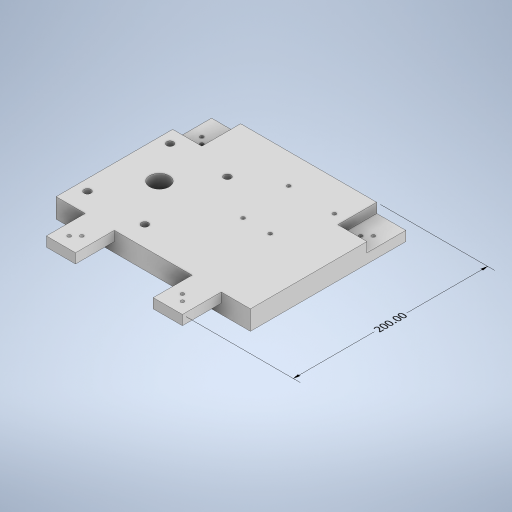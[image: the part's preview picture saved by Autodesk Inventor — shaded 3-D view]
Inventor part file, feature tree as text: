
AUTODESK INVENTOR PART (.ipt)
format: ipt  version: 2023 (Build 270158000, 158)  size: 358,912 bytes
history: native  units: mm
features: sketch x7, extrude x4, other x3, hole x3
ambient origin geometry x8: Origin, YZ Plane, XZ Plane, XY Plane, X Axis, Y Axis, Z Axis, Center Point
bodies: Body1 (feature_tree)
feature tree (17):
  other  "Sólido1"
  other  "Anotaciones"
  extrude  "Extrusión1"  Depth=160.0mm
  extrude  "Extrusión2"  Depth=30.0mm
  hole  "Agujero1"  [1 undecoded]
  extrude  "Extrusión3"  Depth=11.75mm
  hole  "Agujero2"  [1 undecoded]
  hole  "Agujero3"  [1 undecoded]
  extrude  "Extrusión4"  Depth=40.0mm TaperAngle=0.0deg
  sketch  "Boceto1"  dims[d0=200.0mm d1=160.0mm]
  sketch  "Boceto2"  dims[d2=20.0mm d3=0.0mm d4=30.0mm]
  sketch  "Boceto3"  dims[d5=40.0mm d6=10.0mm d7=0.0mm]
  sketch  "Boceto4"  dims[d23=21.75mm d24=11.75mm]
  sketch  "Boceto5"  dims[d26=11.75mm]
  sketch  "Boceto6"  dims[d27=3.5mm d28=6.0mm d29=4.0mm d30=2.0mm d31=90.0deg d32=8.0mm d33=20.594885mm d34=30.0mm]
  sketch  "Boceto7"  dims[d35=10.0mm d36=30.0mm d37=40.0mm d38=0.0mm d39=10.0mm d40=10.0mm d41=40.0mm d42=0.0mm d43=6.5mm d44=6.5mm d45=3.5mm d46=3.5mm d47=11.749873mm d48=11.75mm d49=0.0mm d50=11.75mm d51=0.0mm d52=3.5mm d53=6.0mm d54=4.0mm d55=2.0mm d56=90.0deg d57=8.0mm d58=20.594885mm d59=7.0mm d60=7.0mm d61=7.0mm d62=39.0mm d63=46.0mm d64=59.0mm d65=46.0mm d66=39.0mm d67=59.0mm d68=52.0mm d69=70.0mm d70=22.0mm d71=42.0mm d72=3.5mm d73=3.5mm d74=3.5mm d75=3.5mm d76=3.5mm d77=6.0mm d78=4.0mm d79=2.0mm d80=90.0deg d81=8.0mm d82=20.594885mm d83=7.0mm d84=7.0mm d85=7.0mm d86=39.0mm d87=46.0mm d88=59.0mm d89=46.0mm d90=39.0mm d91=59.0mm d92=20.0mm d93=0.0mm d97=40.000127mm d94=6.100674mm d95=2.550465mm d96=200.0mm d98=14.3117mm d99=0.75mm d100=20.594885mm d101=0.0625mm d102=0.75mm d103=0.375mm]
  other  "Cota lineal 1"
note: 3 required parameter values undecoded (feature->parameter linkage not recoverable at this tier; creation-order binding heuristic only, values carry confidence <= 0.55)
